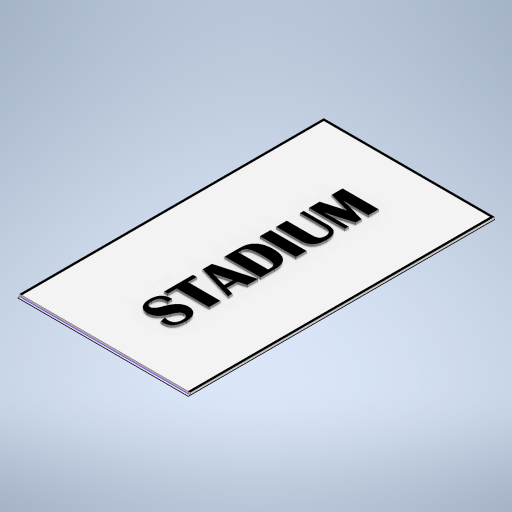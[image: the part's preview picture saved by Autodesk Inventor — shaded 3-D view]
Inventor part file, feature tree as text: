
AUTODESK INVENTOR PART (.ipt)
format: ipt  version: 2024.1 (Build 281209000, 209)  size: 386,560 bytes
history: native  units: in
note: dims shown in document units (in); Inventor stores cm internally (conversion verified against a paired STEP export)
features: extrude x4, sketch x2
ambient origin geometry x8: Origin, YZ Plane, XZ Plane, XY Plane, X Axis, Y Axis, Z Axis, Center Point
bodies: Solid1 (feature_tree), Solid2 (feature_tree), Solid3 (feature_tree)
feature tree (6):
  sketch  "Sketch1"  dims[d3=20.0in d4=0.0in d5=10.0in d6=0.0in]
  extrude  "Extrusion1"  Depth=10.0in TaperAngle=0.0deg
  extrude  "Extrusion2"  Depth=30.0in TaperAngle=0.0deg
  extrude  "Extrusion3"  Depth=0.5in
  extrude  "Extrusion4"  Depth=0.0344in
  sketch  "Sketch2"  dims[d7=10.0in d8=0.0in d9=30.0in d10=0.0in d11=0.5in d12=0.0344in]
